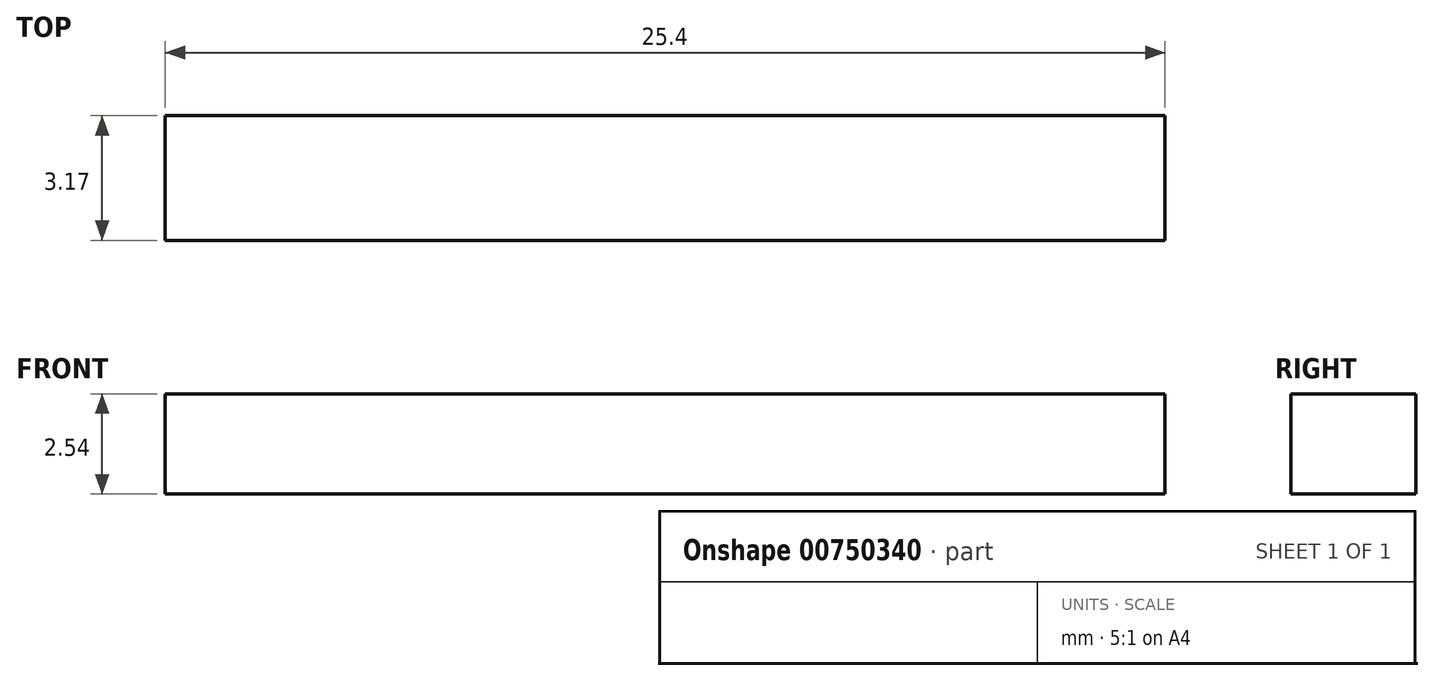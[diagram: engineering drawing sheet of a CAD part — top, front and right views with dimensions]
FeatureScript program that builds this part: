
annotation { "Feature Type Name" : "Feature", "Feature Type Description" : "" }
export const myFeature = defineFeature(function(context is Context, id is Id, definition is map)
    precondition{}
    {
        {
            var Q0;
            Q0=qCreatedBy(makeId("Front.planeOp"),FACE);
            var sketch = newSketch(context, id + "F0", { "sketchPlane" : qUnion([Q0])});
            skLineSegment(sketch, "E0.bottom", {"start": v(-7.39, 3.03) * mm, "end": v(18.01, 3.03) * mm});
            skLineSegment(sketch, "E0.top", {"start": v(-7.39, 0.5) * mm, "end": v(18.01, 0.5) * mm});
            skLineSegment(sketch, "E0.left", {"start": v(-7.39, 3.03) * mm, "end": v(-7.39, 0.5) * mm});
            skLineSegment(sketch, "E0.right", {"start": v(18.01, 3.03) * mm, "end": v(18.01, 0.5) * mm});
            skSolve(sketch);
        }
        {
            var Q0;
            Q0=makeQuery(id+"F0.imprint","IMPRINT",FACE,{"disambiguationData":[TD([[makeQuery(id+"F0.imprint","IMPRINT",EDGE,{"derivedFrom":sQuery(id+"F0.wireOp",EDGE,"E0.bottom")}),-1.0]])]});
            extrude(context, id + "F1", {"entities" : qUnion([Q0]), "depth" : 3.17 * mm, "offsetDistance" : 25.4 * mm});
        }
    });
